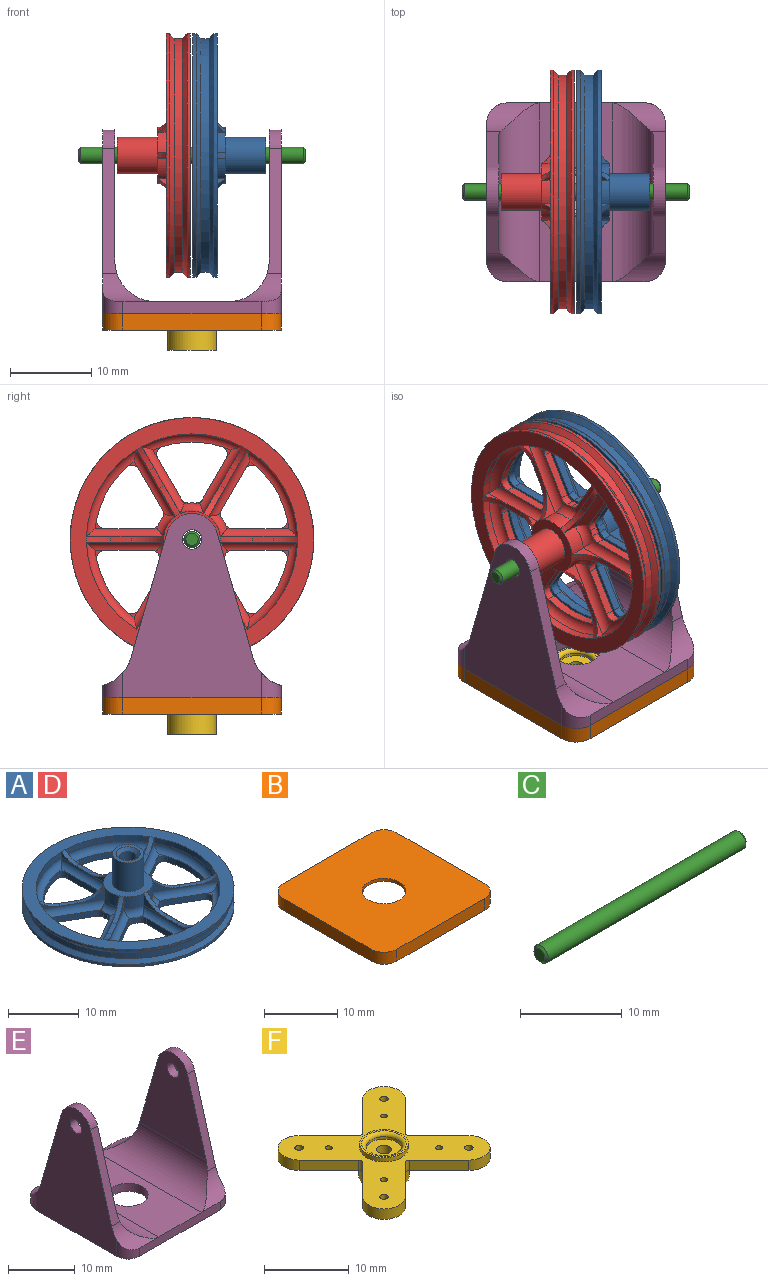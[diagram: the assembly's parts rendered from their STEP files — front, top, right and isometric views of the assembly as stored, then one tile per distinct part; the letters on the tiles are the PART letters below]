
ASSEMBLY  parts=6 mates=6
PART A: 167 faces, bbox 30.1x30.1x9.1 mm
  f0: plane 2.62x1.52mm, normal (-0.5,-0.87,0), area 1mm2, adj f59,f89,f155
  f1: plane 3.55x2.08mm, normal (0.5,0.87,0), area 2.4mm2, adj f40,f88,f158
  f2: plane 3.02x1.02mm, normal (-1,0,0), area 1mm2, adj f35,f86,f161
  f3: plane 1.07x0.38mm, normal (0,0,1), area 0.1mm2, adj f136,f158,f159
  f4: plane 0.9x0.57mm, normal (0,0,1), area 0.1mm2, adj f130,f159,f161
  f5: plane 1.21x1.18mm, normal (0,0,1), area 0.3mm2, adj f132,f160,f161
  f6: plane 4.08x2.08mm, normal (1,0,0), area 2.4mm2, adj f39,f87,f140
  f7: plane 2.62x1.52mm, normal (-0.5,0.87,0), area 1mm2, adj f34,f84,f139
  f8: plane 3.55x2.08mm, normal (0.5,-0.87,0), area 2.4mm2, adj f38,f85,f144
  f9: plane 2.62x1.52mm, normal (0.5,0.87,0), area 1mm2, adj f33,f83,f143
  f10: plane 3.55x2.08mm, normal (-0.5,-0.87,0), area 2.4mm2, adj f37,f82,f148
  f11: plane 3.02x1.02mm, normal (1,0,0), area 1mm2, adj f32,f81,f147
  f12: plane 4.08x2.08mm, normal (-1,0,0), area 2.4mm2, adj f36,f80,f152
  f13: plane 2.62x1.52mm, normal (0.5,-0.87,0), area 1mm2, adj f31,f79,f151
  f14: plane 3.55x2.08mm, normal (-0.5,0.87,0), area 2.4mm2, adj f56,f78,f156
  f15: plane 1.45x1.15mm, normal (0,0,1), area 0.3mm2, adj f126,f154,f156
  f16: plane 0.95x0.59mm, normal (0,0,1), area 0.1mm2, adj f128,f156,f157
  f17: plane 0.95x0.59mm, normal (0,0,1), area 0.1mm2, adj f122,f155,f157
  f18: plane 1.07x0.38mm, normal (0,0,1), area 0.1mm2, adj f98,f151,f153
  f19: plane 1.54x1.02mm, normal (0,0,1), area 0.3mm2, adj f100,f150,f151
  f20: plane 1.21x1.18mm, normal (0,0,1), area 0.3mm2, adj f102,f150,f152
  f21: plane 0.9x0.57mm, normal (0,0,1), area 0.1mm2, adj f90,f147,f149
  f22: plane 1.21x1.18mm, normal (0,0,1), area 0.3mm2, adj f92,f146,f147
  f23: plane 1.54x1.02mm, normal (0,0,1), area 0.3mm2, adj f94,f146,f148
  f24: plane 0.95x0.59mm, normal (0,0,1), area 0.1mm2, adj f106,f143,f145
  f25: plane 1.45x1.15mm, normal (0,0,1), area 0.3mm2, adj f108,f142,f143
  f26: plane 1.45x1.15mm, normal (0,0,1), area 0.3mm2, adj f110,f142,f144
  f27: plane 1.07x0.38mm, normal (0,0,1), area 0.1mm2, adj f120,f139,f141
  f28: plane 1.54x1.02mm, normal (0,0,1), area 0.3mm2, adj f114,f138,f139
  f29: plane 1.21x1.18mm, normal (0,0,1), area 0.3mm2, adj f116,f138,f140
  f30: plane 0.9x0.57mm, normal (0,0,1), area 0.1mm2, adj f118,f140,f141
  f31: cylinder r=13mm len=10.73mm, axis (0,0,-1), area 12.9mm2, adj f13,f46,f70,f150
  f32: cylinder r=13mm len=10.73mm, axis (0,0,-1), area 12.9mm2, adj f11,f46,f73,f146
  f33: cylinder r=13mm len=12.39mm, axis (0,0,-1), area 12.9mm2, adj f9,f46,f75,f142
  f34: cylinder r=13mm len=10.73mm, axis (0,0,-1), area 12.9mm2, adj f7,f46,f60,f138
  f35: cylinder r=13mm len=10.73mm, axis (0,0,-1), area 12.9mm2, adj f2,f46,f63,f160
  f36: cylinder r=3.5mm len=2.49mm, axis (0,0,1), area 5.9mm2, adj f12,f58,f66,f153
  f37: cylinder r=3.5mm len=2.49mm, axis (0,0,1), area 5.9mm2, adj f10,f58,f69,f149
  f38: cylinder r=3.5mm len=2.88mm, axis (0,0,1), area 5.9mm2, adj f8,f58,f72,f145
  f39: cylinder r=3.5mm len=2.49mm, axis (0,0,1), area 5.9mm2, adj f6,f58,f76,f141
  f40: cylinder r=3.5mm len=2.49mm, axis (0,0,1), area 5.9mm2, adj f1,f58,f61,f159
  f41: plane 0.95x0.59mm, normal (0,0,1), area 0.1mm2, adj f112,f144,f145
  f42: plane 1.07x0.38mm, normal (0,0,1), area 0.1mm2, adj f96,f148,f149
  f43: plane 0.9x0.57mm, normal (0,0,1), area 0.1mm2, adj f104,f152,f153
  f44: plane 1.45x1.15mm, normal (0,0,1), area 0.3mm2, adj f124,f154,f155
  f45: plane 1.54x1.02mm, normal (0,0,1), area 0.3mm2, adj f134,f158,f160
  f46: plane 30x30mm, normal (0,0,1), area 175.9mm2, adj f31,f32,f33,f34,f35,f57,f59,f79
  f47: cylinder r=1.2mm len=8mm, axis (0,0,-1), area 60.3mm2, adj f51,f52
  f48: cylinder r=15mm len=30mm, axis (0,0,1), area 37.7mm2, adj f49,f50
  f49: plane 30x30mm, normal (0,0,-1), area 436mm2, adj f48,f51,f90,f91,f92,f93,f94,f95
  f50: cone r=15mm half-angle=45deg, axis (0,0,-1), area 78.4mm2, adj f48,f162
  f51: cone r=1.7mm half-angle=45deg, axis (0,0,-1), area 6.4mm2, adj f47,f49
  f52: cone r=1.2mm half-angle=45deg, axis (0,0,1), area 6.4mm2, adj f47,f54
  f53: cone r=14.4mm half-angle=45deg, axis (0,0,1), area 78.4mm2, adj f57,f162
  f54: plane 4.5x4.5mm, normal (0,0,1), area 6.8mm2, adj f52,f55
  f55: cylinder r=2.25mm len=5mm, axis (0,0,-1), area 70.7mm2, adj f54,f58
  f56: cylinder r=3.5mm len=2.88mm, axis (0,0,1), area 5.9mm2, adj f14,f58,f64,f157
  f57: cylinder r=15mm len=30mm, axis (0,0,1), area 37.7mm2, adj f46,f53
  f58: plane 7x7mm, normal (0,0,1), area 22.6mm2, adj f36,f37,f38,f39,f40,f55,f56,f78
  f59: cylinder r=13mm len=12.39mm, axis (0,0,-1), area 12.9mm2, adj f0,f46,f67,f154
  f60: plane 3.02x1.02mm, normal (1,0,0), area 1mm2, adj f34,f86,f140
  f61: plane 4.08x2.07mm, normal (-1,0,0), area 2.4mm2, adj f40,f87,f161
  f62: plane 2.51x0.7mm, normal (0,0,1), area 1.8mm2, adj f86,f87,f140,f161
  f63: plane 2.62x1.52mm, normal (0.5,0.87,0), area 1mm2, adj f35,f89,f158
  f64: plane 3.55x2.08mm, normal (-0.5,-0.87,0), area 2.4mm2, adj f56,f88,f155
  f65: plane 2.52x1.86mm, normal (0,0,1), area 1.8mm2, adj f88,f89,f155,f158
  f66: plane 3.55x2.08mm, normal (0.5,-0.87,0), area 2.4mm2, adj f36,f78,f151
  f67: plane 2.62x1.52mm, normal (-0.5,0.87,0), area 1mm2, adj f59,f79,f156
  f68: plane 2.52x1.86mm, normal (0,0,1), area 1.8mm2, adj f78,f79,f151,f156
  f69: plane 4.08x2.07mm, normal (1,0,0), area 2.4mm2, adj f37,f80,f147
  f70: plane 3.02x1.02mm, normal (-1,0,0), area 1mm2, adj f31,f81,f152
  f71: plane 2.51x0.7mm, normal (0,0,1), area 1.8mm2, adj f80,f81,f147,f152
  f72: plane 3.55x2.08mm, normal (0.5,0.87,0), area 2.4mm2, adj f38,f82,f143
  f73: plane 2.62x1.52mm, normal (-0.5,-0.87,0), area 1mm2, adj f32,f83,f148
  f74: plane 2.52x1.86mm, normal (0,0,1), area 1.8mm2, adj f82,f83,f143,f148
  f75: plane 2.62x1.52mm, normal (0.5,-0.87,0), area 1mm2, adj f33,f84,f144
  f76: plane 3.55x2.08mm, normal (-0.5,0.87,0), area 2.4mm2, adj f39,f85,f139
  f77: plane 2.52x1.86mm, normal (0,0,1), area 1.8mm2, adj f84,f85,f139,f144
  f78: torus R=7.5mm, axis (0,0,1), area 3.5mm2, adj f14,f58,f66,f68
  f79: torus R=10mm, axis (0,0,-1), area 2.3mm2, adj f13,f46,f67,f68
  f80: torus R=7.5mm, axis (0,0,1), area 3.5mm2, adj f12,f58,f69,f71
  f81: torus R=10mm, axis (0,0,-1), area 2.3mm2, adj f11,f46,f70,f71
  f82: torus R=7.5mm, axis (0,0,1), area 3.5mm2, adj f10,f58,f72,f74
  f83: torus R=10mm, axis (0,0,-1), area 2.3mm2, adj f9,f46,f73,f74
  f84: torus R=10mm, axis (0,0,-1), area 2.3mm2, adj f7,f46,f75,f77
  f85: torus R=7.5mm, axis (0,0,1), area 3.5mm2, adj f8,f58,f76,f77
  f86: torus R=10mm, axis (0,0,-1), area 2.3mm2, adj f2,f46,f60,f62
  f87: torus R=7.5mm, axis (0,0,1), area 3.5mm2, adj f6,f58,f61,f62
  f88: torus R=7.5mm, axis (0,0,1), area 3.5mm2, adj f1,f58,f64,f65
  f89: torus R=10mm, axis (0,0,-1), area 2.3mm2, adj f0,f46,f63,f65
  f90: cylinder r=1mm len=1mm, axis (0,0,1), area 1.1mm2, adj f21,f49,f91,f97
  f91: plane 5.77x1mm, normal (1,0,0), area 5.8mm2, adj f49,f90,f92,f147
  f92: cylinder r=1mm len=1.21mm, axis (0,0,1), area 1.8mm2, adj f22,f49,f91,f93
  f93: cylinder r=12mm len=6.31mm, axis (0,0,1), area 7.4mm2, adj f49,f92,f94,f146
  f94: cylinder r=1mm len=1.54mm, axis (0,0,1), area 1.8mm2, adj f23,f49,f93,f95
  f95: plane 5x2.89mm, normal (-0.5,-0.87,0), area 5.8mm2, adj f49,f94,f96,f148
  f96: cylinder r=1mm len=1.07mm, axis (0,0,1), area 1.1mm2, adj f42,f49,f95,f97
  f97: cylinder r=4.5mm len=1mm, axis (0,0,1), area 0.7mm2, adj f49,f90,f96,f149
  f98: cylinder r=1mm len=1.07mm, axis (0,0,1), area 1.1mm2, adj f18,f49,f99,f105
  f99: plane 5x2.89mm, normal (0.5,-0.87,0), area 5.8mm2, adj f49,f98,f100,f151
  f100: cylinder r=1mm len=1.54mm, axis (0,0,1), area 1.8mm2, adj f19,f49,f99,f101
  f101: cylinder r=12mm len=6.31mm, axis (0,0,1), area 7.4mm2, adj f49,f100,f102,f150
  f102: cylinder r=1mm len=1.21mm, axis (0,0,1), area 1.8mm2, adj f20,f49,f101,f103
  f103: plane 5.77x1mm, normal (-1,0,0), area 5.8mm2, adj f49,f102,f104,f152
  f104: cylinder r=1mm len=1mm, axis (0,0,1), area 1.1mm2, adj f43,f49,f103,f105
  f105: cylinder r=4.5mm len=1mm, axis (0,0,1), area 0.7mm2, adj f49,f98,f104,f153
  f106: cylinder r=1mm len=1mm, axis (0,0,1), area 1.1mm2, adj f24,f49,f107,f113
  f107: plane 5x2.89mm, normal (0.5,0.87,0), area 5.8mm2, adj f49,f106,f108,f143
  f108: cylinder r=1mm len=1.45mm, axis (0,0,1), area 1.8mm2, adj f25,f49,f107,f109
  f109: cylinder r=12mm len=7.28mm, axis (0,0,1), area 7.4mm2, adj f49,f108,f110,f142
  f110: cylinder r=1mm len=1.45mm, axis (0,0,1), area 1.8mm2, adj f26,f49,f109,f111
  f111: plane 5x2.89mm, normal (0.5,-0.87,0), area 5.8mm2, adj f49,f110,f112,f144
  f112: cylinder r=1mm len=1mm, axis (0,0,1), area 1.1mm2, adj f41,f49,f111,f113
  f113: cylinder r=4.5mm len=1mm, axis (0,0,1), area 0.7mm2, adj f49,f106,f112,f145
  f114: cylinder r=1mm len=1.54mm, axis (0,0,1), area 1.8mm2, adj f28,f49,f115,f121
  f115: cylinder r=12mm len=6.31mm, axis (0,0,1), area 7.4mm2, adj f49,f114,f116,f138
  f116: cylinder r=1mm len=1.21mm, axis (0,0,1), area 1.8mm2, adj f29,f49,f115,f117
  f117: plane 5.77x1mm, normal (1,0,0), area 5.8mm2, adj f49,f116,f118,f140
  f118: cylinder r=1mm len=1mm, axis (0,0,1), area 1.1mm2, adj f30,f49,f117,f119
  f119: cylinder r=4.5mm len=1mm, axis (0,0,1), area 0.7mm2, adj f49,f118,f120,f141
  f120: cylinder r=1mm len=1.07mm, axis (0,0,1), area 1.1mm2, adj f27,f49,f119,f121
  f121: plane 5x2.89mm, normal (-0.5,0.87,0), area 5.8mm2, adj f49,f114,f120,f139
  f122: cylinder r=1mm len=1mm, axis (0,0,1), area 1.1mm2, adj f17,f49,f123,f129
  f123: plane 5x2.89mm, normal (-0.5,-0.87,0), area 5.8mm2, adj f49,f122,f124,f155
  f124: cylinder r=1mm len=1.45mm, axis (0,0,1), area 1.8mm2, adj f44,f49,f123,f125
  f125: cylinder r=12mm len=7.28mm, axis (0,0,1), area 7.4mm2, adj f49,f124,f126,f154
  f126: cylinder r=1mm len=1.45mm, axis (0,0,1), area 1.8mm2, adj f15,f49,f125,f127
  f127: plane 5x2.89mm, normal (-0.5,0.87,0), area 5.8mm2, adj f49,f126,f128,f156
  f128: cylinder r=1mm len=1mm, axis (0,0,1), area 1.1mm2, adj f16,f49,f127,f129
  f129: cylinder r=4.5mm len=1mm, axis (0,0,1), area 0.7mm2, adj f49,f122,f128,f157
  f130: cylinder r=1mm len=1mm, axis (0,0,1), area 1.1mm2, adj f4,f49,f131,f137
  f131: plane 5.77x1mm, normal (-1,0,0), area 5.8mm2, adj f49,f130,f132,f161
  f132: cylinder r=1mm len=1.21mm, axis (0,0,1), area 1.8mm2, adj f5,f49,f131,f133
  f133: cylinder r=12mm len=6.31mm, axis (0,0,1), area 7.4mm2, adj f49,f132,f134,f160
  f134: cylinder r=1mm len=1.54mm, axis (0,0,1), area 1.8mm2, adj f45,f49,f133,f135
  f135: plane 5x2.89mm, normal (0.5,0.87,0), area 5.8mm2, adj f49,f134,f136,f158
  f136: cylinder r=1mm len=1.07mm, axis (0,0,1), area 1.1mm2, adj f3,f49,f135,f137
  f137: cylinder r=4.5mm len=1mm, axis (0,0,1), area 0.7mm2, adj f49,f130,f136,f159
  f138: torus R=12mm, axis (0,0,-1), area 18.5mm2, adj f28,f29,f34,f115,f139,f140
  f139: cylinder r=1mm len=8.74mm, axis (0.87,0.5,0), area 13.9mm2, adj f7,f27,f28,f76,f77,f121,f138,f141
  f140: cylinder r=1mm len=9.51mm, axis (0,-1,0), area 13.9mm2, adj f6,f29,f30,f60,f62,f117,f138,f141
  f141: torus R=4.5mm, axis (0,0,-1), area 4.1mm2, adj f27,f30,f39,f119,f139,f140
  f142: torus R=12mm, axis (0,0,-1), area 18.5mm2, adj f25,f26,f33,f109,f143,f144
  f143: cylinder r=1mm len=8.74mm, axis (0.87,-0.5,0), area 13.9mm2, adj f9,f24,f25,f72,f74,f107,f142,f145
  f144: cylinder r=1mm len=8.74mm, axis (-0.87,-0.5,0), area 13.9mm2, adj f8,f26,f41,f75,f77,f111,f142,f145
  f145: torus R=4.5mm, axis (0,0,-1), area 4.1mm2, adj f24,f38,f41,f113,f143,f144
  f146: torus R=12mm, axis (0,0,-1), area 18.5mm2, adj f22,f23,f32,f93,f147,f148
  f147: cylinder r=1mm len=9.51mm, axis (0,-1,0), area 13.9mm2, adj f11,f21,f22,f69,f71,f91,f146,f149
  f148: cylinder r=1mm len=8.74mm, axis (-0.87,0.5,0), area 13.9mm2, adj f10,f23,f42,f73,f74,f95,f146,f149
  f149: torus R=4.5mm, axis (0,0,-1), area 4.1mm2, adj f21,f37,f42,f97,f147,f148
  f150: torus R=12mm, axis (0,0,-1), area 18.5mm2, adj f19,f20,f31,f101,f151,f152
  f151: cylinder r=1mm len=8.74mm, axis (-0.87,-0.5,0), area 13.9mm2, adj f13,f18,f19,f66,f68,f99,f150,f153
  f152: cylinder r=1mm len=9.51mm, axis (0,1,0), area 13.9mm2, adj f12,f20,f43,f70,f71,f103,f150,f153
  f153: torus R=4.5mm, axis (0,0,-1), area 4.1mm2, adj f18,f36,f43,f105,f151,f152
  f154: torus R=12mm, axis (0,0,-1), area 18.5mm2, adj f15,f44,f59,f125,f155,f156
  f155: cylinder r=1mm len=8.74mm, axis (-0.87,0.5,0), area 13.9mm2, adj f0,f17,f44,f64,f65,f123,f154,f157
  f156: cylinder r=1mm len=8.74mm, axis (0.87,0.5,0), area 13.9mm2, adj f14,f15,f16,f67,f68,f127,f154,f157
  f157: torus R=4.5mm, axis (0,0,-1), area 4.1mm2, adj f16,f17,f56,f129,f155,f156
  f158: cylinder r=1mm len=8.74mm, axis (0.87,-0.5,0), area 13.9mm2, adj f1,f3,f45,f63,f65,f135,f159,f160
  f159: torus R=4.5mm, axis (0,0,-1), area 4.1mm2, adj f3,f4,f40,f137,f158,f161
  f160: torus R=12mm, axis (0,0,-1), area 18.5mm2, adj f5,f35,f45,f133,f158,f161
  f161: cylinder r=1mm len=9.51mm, axis (0,1,0), area 13.9mm2, adj f2,f4,f5,f61,f62,f131,f159,f160
  f162: cylinder r=14.4mm len=28.8mm, axis (0,0,1), area 90.5mm2, adj f50,f53
  f163: plane 4.5x4.5mm, normal (0,0,1), area 0.7mm2, adj f164,f165
  f164: cylinder r=2.2mm len=4.4mm, axis (0,0,-1), area 13.8mm2, adj f163,f166
  f165: cylinder r=2.25mm len=4.5mm, axis (0,0,1), area 14.1mm2, adj f163,f166
  f166: plane 4.5x4.5mm, normal (0,0,-1), area 0.7mm2, adj f164,f165
PART B: 28 faces, bbox 22x22x2 mm
  f0: cylinder r=3mm len=6mm, axis (0,0,1), area 9.4mm2, adj f10,f11
  f1: cylinder r=2.5mm len=2.5mm, axis (0,0,1), area 7.9mm2, adj f2,f8,f9,f10
  f2: plane 17x2mm, normal (-1,0,0), area 34mm2, adj f1,f3,f9,f10
  f3: cylinder r=2.5mm len=2.5mm, axis (0,0,1), area 7.9mm2, adj f2,f4,f9,f10
  f4: plane 17x2mm, normal (0,1,0), area 34mm2, adj f3,f5,f9,f10
  f5: cylinder r=2.5mm len=2.5mm, axis (0,0,1), area 7.9mm2, adj f4,f6,f9,f10
  f6: plane 17x2mm, normal (1,0,0), area 34mm2, adj f5,f7,f9,f10
  f7: cylinder r=2.5mm len=2.5mm, axis (0,0,1), area 7.9mm2, adj f6,f8,f9,f10
  f8: plane 17x2mm, normal (0,-1,0), area 34mm2, adj f1,f7,f9,f10
  f9: plane 22x22mm, normal (0,0,-1), area 241.3mm2, adj f1,f2,f3,f4,f5,f6,f7,f8
  f10: plane 22x22mm, normal (0,0,1), area 450.4mm2, adj f0,f1,f2,f3,f4,f5,f6,f7
  f11: plane 19.64x19.64mm, normal (0,0,-1), area 209mm2, adj f0,f12,f13,f14,f15,f16,f17,f18
  f12: plane 4.95x4.95mm, normal (0.71,0.71,0), area 10.5mm2, adj f9,f11,f13,f26
  f13: cylinder r=0.25mm len=1.5mm, axis (0,0,1), area 0.6mm2, adj f9,f11,f12,f14
  f14: plane 4.95x4.95mm, normal (0.71,-0.71,0), area 10.5mm2, adj f9,f11,f13,f15
  f15: cylinder r=2.75mm len=4.69mm, axis (0,0,-1), area 13mm2, adj f9,f11,f14,f16
  f16: plane 4.95x4.95mm, normal (-0.71,0.71,0), area 10.5mm2, adj f9,f11,f15,f17
  f17: cylinder r=0.25mm len=1.5mm, axis (0,0,1), area 0.6mm2, adj f9,f11,f16,f18
  f18: plane 4.95x4.95mm, normal (0.71,0.71,0), area 10.5mm2, adj f9,f11,f17,f19
  f19: cylinder r=2.75mm len=4.69mm, axis (0,0,-1), area 13mm2, adj f9,f11,f18,f20
  f20: plane 4.95x4.95mm, normal (-0.71,-0.71,0), area 10.5mm2, adj f9,f11,f19,f21
  f21: cylinder r=0.25mm len=1.5mm, axis (0,0,1), area 0.6mm2, adj f9,f11,f20,f22
  f22: plane 4.95x4.95mm, normal (-0.71,0.71,0), area 10.5mm2, adj f9,f11,f21,f23
  f23: cylinder r=2.75mm len=4.69mm, axis (0,0,-1), area 13mm2, adj f9,f11,f22,f24
  f24: plane 4.95x4.95mm, normal (0.71,-0.71,0), area 10.5mm2, adj f9,f11,f23,f25
  f25: cylinder r=0.25mm len=1.5mm, axis (0,0,1), area 0.6mm2, adj f9,f11,f24,f27
  f26: cylinder r=2.75mm len=4.69mm, axis (0,0,-1), area 13mm2, adj f9,f11,f12,f27
  f27: plane 4.95x4.95mm, normal (-0.71,-0.71,0), area 10.5mm2, adj f9,f11,f25,f26
PART C: 5 faces, bbox 28x2x2 mm
  f0: cylinder r=1mm len=27.5mm, axis (-1,0,0), area 172.8mm2, adj f3,f4
  f1: plane 1.5x1.5mm, normal (1,0,0), area 1.8mm2, adj f3
  f2: plane 1.5x1.5mm, normal (-1,0,0), area 1.8mm2, adj f4
  f3: cone r=0.75mm half-angle=45deg, axis (-1,0,0), area 1.9mm2, adj f0,f1
  f4: cone r=1mm half-angle=45deg, axis (1,0,0), area 1.9mm2, adj f0,f2
PART D: same geometry as A
PART E: 27 faces, bbox 22x22x22.7 mm
  f0: plane 22.7x17mm, normal (1,0,0), area 251.3mm2, adj f7,f8,f12,f13,f14,f15,f16,f24
  f1: plane 22.7x17mm, normal (-1,0,0), area 251.3mm2, adj f5,f10,f12,f17,f18,f19,f20,f21
  f2: plane 16.2x14.13mm, normal (1,0,0), area 146.7mm2, adj f17,f18,f19,f20,f22
  f3: plane 16.2x14.13mm, normal (-1,0,0), area 146.7mm2, adj f13,f14,f15,f16,f25
  f4: plane 22x9mm, normal (0,0,1), area 169.7mm2, adj f6,f9,f11,f22,f25
  f5: cylinder r=2.5mm len=3.09mm, axis (0,0,-1), area 7.6mm2, adj f1,f6,f12,f21
  f6: plane 17x1.5mm, normal (0,-1,0), area 25.5mm2, adj f4,f5,f7,f12,f21,f26
  f7: cylinder r=2.5mm len=3.09mm, axis (0,0,-1), area 7.6mm2, adj f0,f6,f12,f26
  f8: cylinder r=2.5mm len=3.09mm, axis (0,0,-1), area 7.6mm2, adj f0,f9,f12,f24
  f9: plane 17x1.5mm, normal (0,1,0), area 25.5mm2, adj f4,f8,f10,f12,f23,f24
  f10: cylinder r=2.5mm len=3.09mm, axis (0,0,-1), area 7.6mm2, adj f1,f9,f12,f23
  f11: cylinder r=3mm len=6mm, axis (0,0,-1), area 28.3mm2, adj f4,f12
  f12: plane 22x22mm, normal (0,0,-1), area 450.4mm2, adj f0,f1,f5,f6,f7,f8,f9,f10
  f13: plane 15.45x4.44mm, normal (0,-0.96,0.28), area 24.2mm2, adj f0,f3,f15,f25,f26
  f14: plane 15.45x4.44mm, normal (0,0.96,0.28), area 24.2mm2, adj f0,f3,f15,f24,f25
  f15: cylinder r=3.2mm len=6.15mm, axis (-1,0,0), area 12.4mm2, adj f0,f3,f13,f14
  f16: cylinder r=1.2mm len=2.4mm, axis (-1,0,0), area 11.3mm2, adj f0,f3
  f17: cylinder r=3.2mm len=6.15mm, axis (-1,0,0), area 12.4mm2, adj f1,f2,f18,f19
  f18: plane 15.45x4.44mm, normal (0,-0.96,0.28), area 24.2mm2, adj f1,f2,f17,f21,f22
  f19: plane 15.45x4.44mm, normal (0,0.96,0.28), area 24.2mm2, adj f1,f2,f17,f22,f23
  f20: cylinder r=1.2mm len=2.4mm, axis (-1,0,0), area 11.3mm2, adj f1,f2
  f21: cylinder r=5mm len=6.5mm, axis (-1,0,0), area 15.9mm2, adj f1,f5,f6,f18,f22
  f22: cylinder r=5mm len=22mm, axis (0,1,0), area 138.8mm2, adj f2,f4,f18,f19,f21,f23
  f23: cylinder r=5mm len=6.5mm, axis (-1,0,0), area 15.9mm2, adj f1,f9,f10,f19,f22
  f24: cylinder r=5mm len=6.5mm, axis (-1,0,0), area 15.9mm2, adj f0,f8,f9,f14,f25
  f25: cylinder r=5mm len=22mm, axis (0,-1,0), area 138.8mm2, adj f3,f4,f13,f14,f24,f26
  f26: cylinder r=5mm len=6.5mm, axis (-1,0,0), area 15.9mm2, adj f0,f6,f7,f13,f25
PART F: 36 faces, bbox 19.1x19.1x4.6 mm
  f0: plane 19.14x19.14mm, normal (0,0,1), area 183.4mm2, adj f2,f3,f4,f5,f6,f7,f8,f9
  f1: cylinder r=0.88mm len=1.75mm, axis (0,0,-1), area 6.9mm2, adj f18,f20
  f2: plane 4.95x4.95mm, normal (0.71,-0.71,0), area 10.5mm2, adj f0,f13,f14,f24
  f3: plane 4.95x4.95mm, normal (0.71,0.71,0), area 10.5mm2, adj f0,f4,f14,f24
  f4: cylinder r=2.5mm len=4.27mm, axis (0,0,-1), area 11.8mm2, adj f0,f3,f5,f14
  f5: plane 4.95x4.95mm, normal (-0.71,-0.71,0), area 10.5mm2, adj f0,f4,f14,f25
  f6: plane 4.95x4.95mm, normal (0.71,-0.71,0), area 10.5mm2, adj f0,f7,f14,f25
  f7: cylinder r=2.5mm len=4.27mm, axis (0,0,-1), area 11.8mm2, adj f0,f6,f8,f14
  f8: plane 4.95x4.95mm, normal (-0.71,0.71,0), area 10.5mm2, adj f0,f7,f14,f26
  f9: plane 4.95x4.95mm, normal (-0.71,-0.71,0), area 10.5mm2, adj f0,f10,f14,f26
  f10: cylinder r=2.5mm len=4.27mm, axis (0,0,-1), area 11.8mm2, adj f0,f9,f11,f14
  f11: plane 4.95x4.95mm, normal (0.71,0.71,0), area 10.5mm2, adj f0,f10,f14,f27
  f12: plane 4.95x4.95mm, normal (-0.71,0.71,0), area 10.5mm2, adj f0,f13,f14,f27
  f13: cylinder r=2.5mm len=4.27mm, axis (0,0,-1), area 11.8mm2, adj f0,f2,f12,f14
  f14: plane 19.14x19.14mm, normal (0,0,-1), area 181.1mm2, adj f2,f3,f4,f5,f6,f7,f8,f9
  f15: cylinder r=1.75mm len=3.5mm, axis (0,0,1), area 27.5mm2, adj f17,f18
  f16: cylinder r=3mm len=6mm, axis (0,0,1), area 47.1mm2, adj f14,f17
  f17: plane 6x6mm, normal (0,0,-1), area 18.7mm2, adj f15,f16
  f18: plane 3.5x3.5mm, normal (0,0,-1), area 7.2mm2, adj f1,f15
  f19: cylinder r=2.12mm len=4.25mm, axis (0,0,1), area 4.7mm2, adj f20,f23
  f20: plane 4.25x4.25mm, normal (0,0,1), area 11.8mm2, adj f1,f19
  f21: cylinder r=2.88mm len=5.75mm, axis (0,0,-1), area 10.8mm2, adj f0,f22
  f22: plane 5.75x5.75mm, normal (0,0,1), area 4.3mm2, adj f21,f23
  f23: torus R=2.62mm, axis (0,0,1), area 11.4mm2, adj f19,f22
  f24: cylinder r=0.5mm len=1.5mm, axis (0,0,1), area 1.2mm2, adj f0,f2,f3,f14
  f25: cylinder r=0.5mm len=1.5mm, axis (0,0,1), area 1.2mm2, adj f0,f5,f6,f14
  f26: cylinder r=0.5mm len=1.5mm, axis (0,0,1), area 1.2mm2, adj f0,f8,f9,f14
  f27: cylinder r=0.5mm len=1.5mm, axis (0,0,1), area 1.2mm2, adj f0,f11,f12,f14
  f28: cylinder r=0.4mm len=1.5mm, axis (0,0,1), area 3.8mm2, adj f0,f14
  f29: cylinder r=0.4mm len=1.5mm, axis (0,0,1), area 3.8mm2, adj f0,f14
  f30: cylinder r=0.5mm len=1.5mm, axis (0,0,1), area 4.7mm2, adj f0,f14
  f31: cylinder r=0.4mm len=1.5mm, axis (0,0,1), area 3.8mm2, adj f0,f14
  f32: cylinder r=0.5mm len=1.5mm, axis (0,0,1), area 4.7mm2, adj f0,f14
  f33: cylinder r=0.4mm len=1.5mm, axis (0,0,1), area 3.8mm2, adj f0,f14
  f34: cylinder r=0.5mm len=1.5mm, axis (0,0,1), area 4.7mm2, adj f0,f14
  f35: cylinder r=0.5mm len=1.5mm, axis (0,0,1), area 4.7mm2, adj f0,f14
PLACE A rot(axis=(-0.71,0,-0.71),180deg) t=(-57.13,-44.73,54.95)mm
PLACE B t=(-58.23,-44.73,35.45)mm
PLACE C t=(-72.23,-44.73,54.95)mm
PLACE D rot(axis=(-0.71,0,0.71),180deg) t=(-59.43,-44.73,54.95)mm
PLACE E t=(-58.23,-44.73,35.45)mm
PLACE F t=(-58.23,-44.73,35.45)mm
MATE revolute D.f31 <-> E.f15  axis (-1,0,0) through (-67.43,-44.73,54.95)mm
MATE fastened E.f11 <-> B.f0  axis (0,0,-1) through (-58.23,-44.73,35.45)mm
MATE revolute C.f0 <-> E.f15  axis (1,0,0) through (-44.23,-44.73,54.95)mm
MATE parallel B.f0 <-> E.f11  axis (0,0,1) through (-58.23,-44.73,35.45)mm
MATE revolute A.f31 <-> D.f31  axis (-1,0,0) through (-58.13,-44.73,54.95)mm
MATE parallel B.f0 <-> F.f1  axis (0,0,-1) through (-58.23,-44.73,34.95)mm
